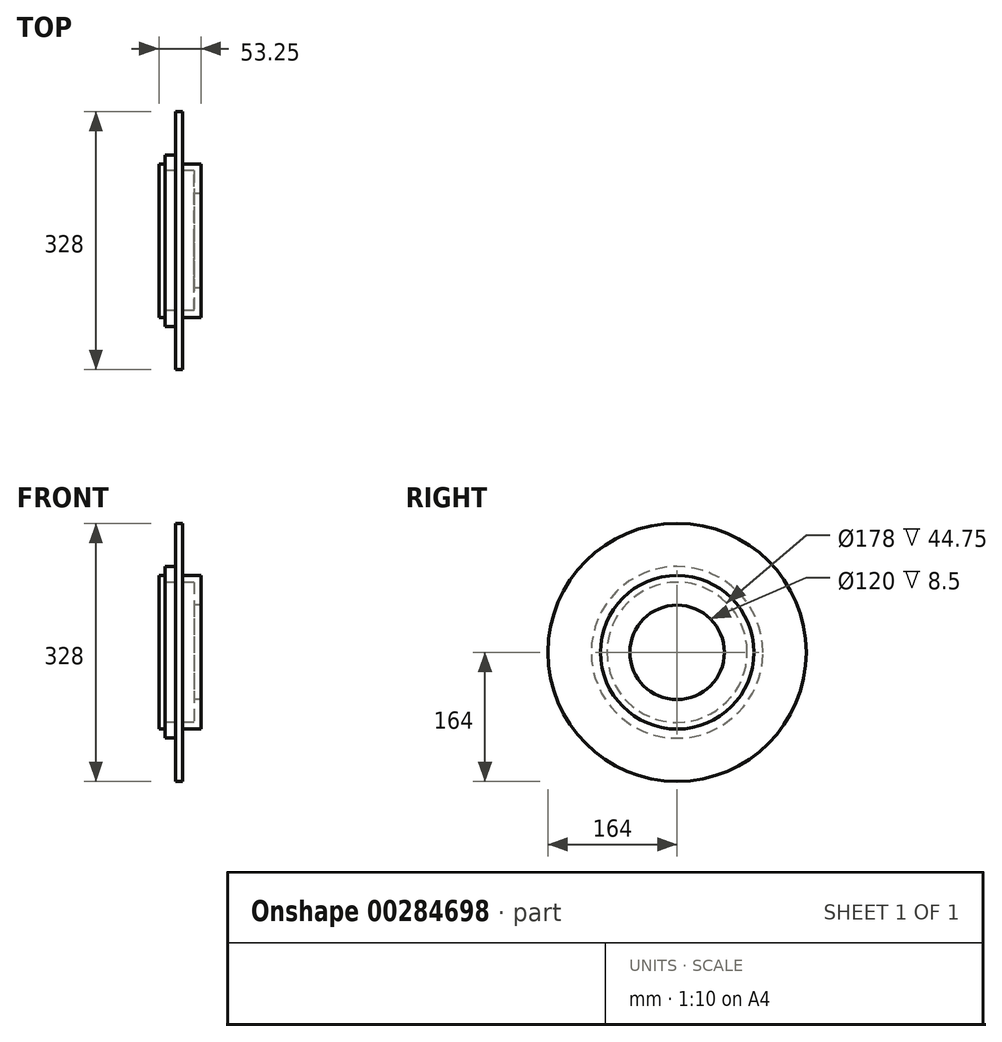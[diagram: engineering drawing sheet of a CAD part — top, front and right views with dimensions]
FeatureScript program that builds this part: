
annotation { "Feature Type Name" : "Feature", "Feature Type Description" : "" }
export const myFeature = defineFeature(function(context is Context, id is Id, definition is map)
    precondition{}
    {
        {
            var Q0;
            Q0=qCreatedBy(makeId("Front.planeOp"),FACE);
            var sketch = newSketch(context, id + "F0", { "sketchPlane" : qUnion([Q0])});
            skLineSegment(sketch, "E0", {"start": v(0, 89) * mm, "end": v(0, 164) * mm});
            skLineSegment(sketch, "E1", {"start": v(0, 164) * mm, "end": v(8, 164) * mm});
            skLineSegment(sketch, "E2", {"start": v(8, 164) * mm, "end": v(8, 89) * mm});
            skLineSegment(sketch, "E3", {"start": v(21, 89) * mm, "end": v(21, 164) * mm});
            skLineSegment(sketch, "E4", {"start": v(21, 164) * mm, "end": v(30, 164) * mm});
            skLineSegment(sketch, "E5", {"start": v(30, 164) * mm, "end": v(30, 89) * mm});
            skPoint(sketch, "E6", {"position": v(30, 97.5) * mm});
            skLineSegment(sketch, "E7", {"start": v(30, 97.5) * mm, "end": v(53.25, 97.5) * mm});
            skLineSegment(sketch, "E8", {"start": v(53.25, 97.5) * mm, "end": v(53.25, 0) * mm});
            skLineSegment(sketch, "E9", {"start": v(30, 89) * mm, "end": v(44.75, 89) * mm});
            skLineSegment(sketch, "E10", {"start": v(44.75, 89) * mm, "end": v(44.75, 0) * mm});
            skLineSegment(sketch, "E11", {"start": v(44.75, 0) * mm, "end": v(53.25, 0) * mm});
            skLineSegment(sketch, "E12", {"start": v(30, 97.5) * mm, "end": v(0, 97.5) * mm});
            skLineSegment(sketch, "E13", {"start": v(0, 97.5) * mm, "end": v(0, 89) * mm});
            skLineSegment(sketch, "E14", {"start": v(0, 89) * mm, "end": v(30, 89) * mm});
            skPoint(sketch, "E15", {"position": v(21, 109) * mm});
            skLineSegment(sketch, "E16", {"start": v(21, 109) * mm, "end": v(8, 109) * mm});
            skPoint(sketch, "E17", {"position": v(44.75, 60) * mm});
            skLineSegment(sketch, "E18", {"start": v(44.75, 60) * mm, "end": v(53.25, 60) * mm});
            skSolve(sketch);
        }
        {
            var Q0;
            {var subQ5=sQuery(id+"F0.wireOp",EDGE,"E0");Q0=makeQuery(id+"F0.imprint","IMPRINT",FACE,{"disambiguationData":[TD([[makeQuery(id+"F0.imprint","IMPRINT",EDGE,{"derivedFrom":subQ5}),-1.0]])]});}
            var Q1;
            {var subQ5=sQuery(id+"F0.wireOp",EDGE,"E13");Q1=makeQuery(id+"F0.imprint","IMPRINT",FACE,{"disambiguationData":[TD([[makeQuery(id+"F0.imprint","IMPRINT",EDGE,{"derivedFrom":subQ5}),1.0]])]});}
            var Q2;
            {var subQ1=sQuery(id+"F0.wireOp",EDGE,"E4");Q2=makeQuery(id+"F0.imprint","IMPRINT",FACE,{"disambiguationData":[TD([[makeQuery(id+"F0.imprint","IMPRINT",EDGE,{"derivedFrom":subQ1}),-1.0]])]});}
            var Q3;
            {var subQ2=sQuery(id+"F0.wireOp",EDGE,"E7");Q3=makeQuery(id+"F0.imprint","IMPRINT",FACE,{"disambiguationData":[TD([[makeQuery(id+"F0.imprint","IMPRINT",EDGE,{"derivedFrom":subQ2}),-1.0]])]});}
            var Q4;
            {var subQ0=sQuery(id+"F0.wireOp",EDGE,"E16");Q4=makeQuery(id+"F0.imprint","IMPRINT",FACE,{"disambiguationData":[TD([[makeQuery(id+"F0.imprint","IMPRINT",EDGE,{"derivedFrom":subQ0}),1.0]])]});}
            var Q5;
            {var subQ0=sQuery(id+"F0.wireOp",EDGE,"E14");var subQ1=sQuery(id+"F0.wireOp",EDGE,"E2");var subQ2=makeQuery(id+"F0.imprint","INTERSECT",VERTEX,{"derivedFrom":[subQ1,subQ0]});Q5=makeQuery(id+"F0.imprint","IMPRINT",FACE,{"disambiguationData":[TD([[makeQuery(id+"F0.imprint","IMPRINT",EDGE,{"disambiguationData":[TD([[subQ2,1.0]])],"derivedFrom":subQ1}),1.0]])]});}
            var Q6;
            {var subQ0=sQuery(id+"F0.wireOp",EDGE,"E14");var subQ1=sQuery(id+"F0.wireOp",EDGE,"E3");var subQ2=makeQuery(id+"F0.imprint","INTERSECT",VERTEX,{"derivedFrom":[subQ1,subQ0]});Q6=makeQuery(id+"F0.imprint","IMPRINT",FACE,{"disambiguationData":[TD([[makeQuery(id+"F0.imprint","IMPRINT",EDGE,{"disambiguationData":[TD([[subQ2,-1.0]])],"derivedFrom":subQ1}),-1.0]])]});}
            var Q7;
            Q7=sQuery(id+"F0.wireOp",EDGE,"E11");
            revolve(context, id + "F1", {"entities" : qUnion([Q0, Q1, Q2, Q3, Q4, Q5, Q6]), "axis" : qUnion([Q7]), "revolveType" : RevolveType.FULL});
        }
    });
